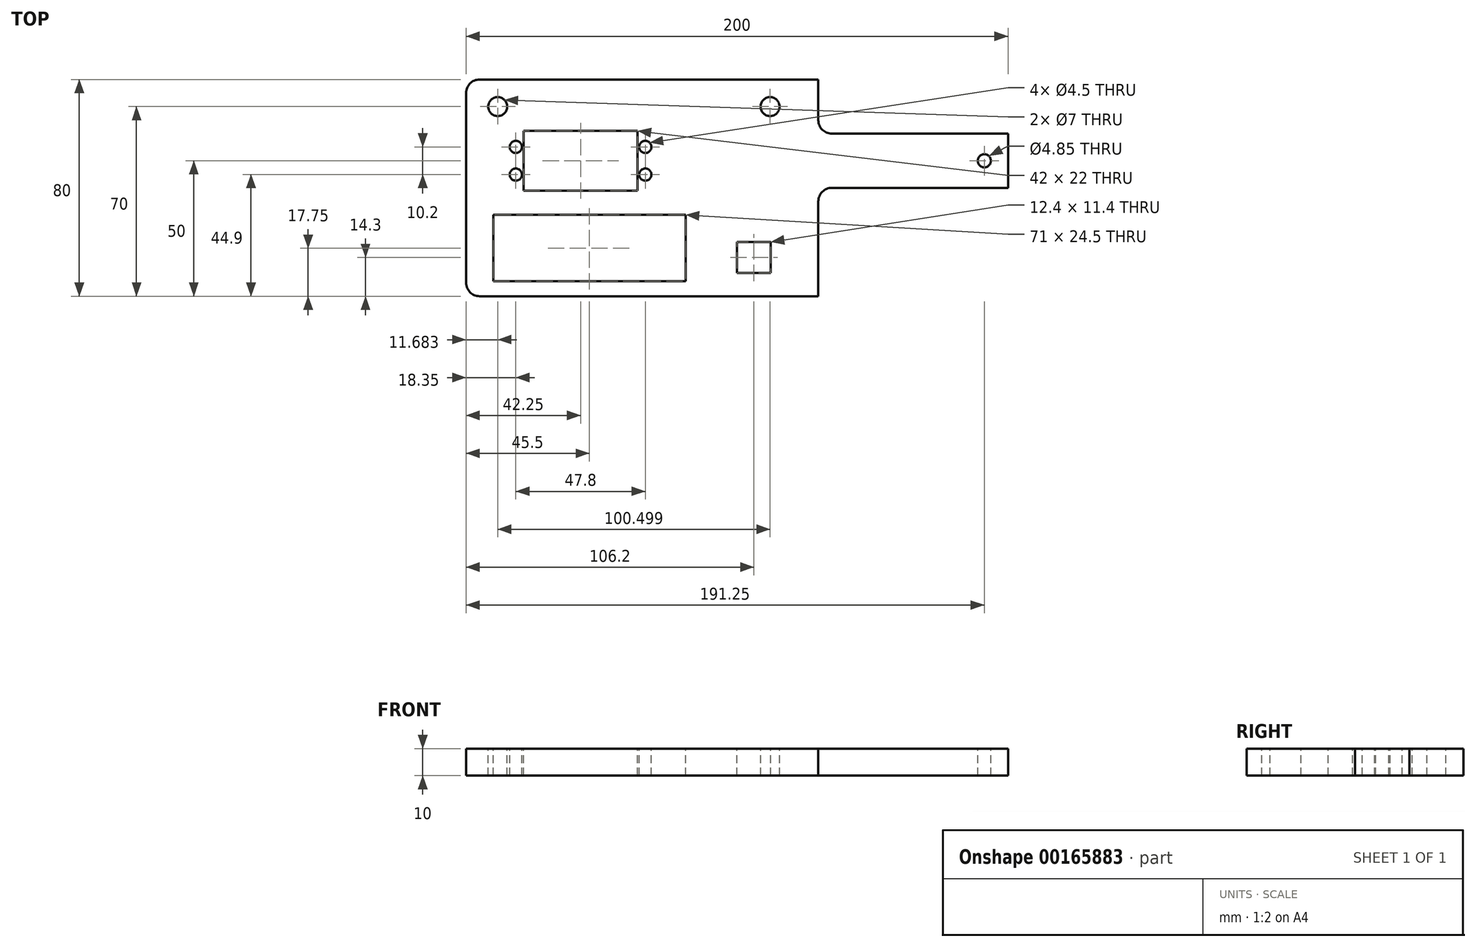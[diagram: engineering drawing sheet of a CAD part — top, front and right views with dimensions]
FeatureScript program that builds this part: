
annotation { "Feature Type Name" : "Feature", "Feature Type Description" : "" }
export const myFeature = defineFeature(function(context is Context, id is Id, definition is map)
    precondition{}
    {
        {
            var Q0;
            Q0=qCreatedBy(makeId("Top.planeOp"),FACE);
            var sketch = newSketch(context, id + "F0", { "sketchPlane" : qUnion([Q0])});
            skLineSegment(sketch, "E0.bottom", {"start": v(100, -40) * mm, "end": v(-100, -40) * mm});
            skLineSegment(sketch, "E0.top", {"start": v(100, 40) * mm, "end": v(-100, 40) * mm});
            skLineSegment(sketch, "E0.left", {"start": v(100, -40) * mm, "end": v(100, 40) * mm});
            skLineSegment(sketch, "E0.right", {"start": v(-100, -40) * mm, "end": v(-100, 40) * mm});
            skPoint(sketch, "E0.middle", {"position": v(0, 0) * mm});
            skSolve(sketch);
        }
        {
            var Q0;
            Q0=makeQuery(id+"F0.imprint","IMPRINT",FACE,{"disambiguationData":[TD([[makeQuery(id+"F0.imprint","IMPRINT",EDGE,{"derivedFrom":sQuery(id+"F0.wireOp",EDGE,"E0.bottom")}),-1.0]])]});
            extrude(context, id + "F1", {"entities" : qUnion([Q0]), "depth" : 10 * mm});
        }
        {
            var Q0;
            Q0=makeQuery(id+"F1.opExtrude","CAP_FACE",FACE,{"disambiguationData":[OSD([sQuery(id+"F0.wireOp",EDGE,"E0.bottom"),sQuery(id+"F0.wireOp",EDGE,"E0.top"),sQuery(id+"F0.wireOp",EDGE,"E0.left"),sQuery(id+"F0.wireOp",EDGE,"E0.right")])],"isStart":false});
            var sketch = newSketch(context, id + "F2", { "sketchPlane" : qUnion([Q0])});
            skLineSegment(sketch, "E1.bottom", {"start": v(-78.75, -1) * mm, "end": v(-36.75, -1) * mm});
            skLineSegment(sketch, "E1.top", {"start": v(-78.75, 21) * mm, "end": v(-36.75, 21) * mm});
            skLineSegment(sketch, "E1.left", {"start": v(-78.75, -1) * mm, "end": v(-78.75, 21) * mm});
            skLineSegment(sketch, "E1.right", {"start": v(-36.75, -1) * mm, "end": v(-36.75, 21) * mm});
            skPoint(sketch, "E1.middle", {"position": v(-57.75, 10) * mm});
            skSolve(sketch);
        }
        {
            var Q0;
            Q0=makeQuery(id+"F2.imprint","IMPRINT",FACE,{"disambiguationData":[TD([[makeQuery(id+"F2.imprint","IMPRINT",EDGE,{"derivedFrom":sQuery(id+"F2.wireOp",EDGE,"E1.bottom")}),1.0]])]});
            extrude(context, id + "F3", {"entities" : qUnion([Q0]), "operationType" : NewBodyOperationType.REMOVE, "endBound" : BoundingType.THROUGH_ALL, "oppositeDirection" : true, "depth" : 25 * mm});
        }
        {
            var Q0;
            Q0=makeQuery(id+"F1.opExtrude","CAP_FACE",FACE,{"disambiguationData":[OSD([sQuery(id+"F0.wireOp",EDGE,"E0.bottom"),sQuery(id+"F0.wireOp",EDGE,"E0.top"),sQuery(id+"F0.wireOp",EDGE,"E0.left"),sQuery(id+"F0.wireOp",EDGE,"E0.right")])],"isStart":false});
            var sketch = newSketch(context, id + "F4", { "sketchPlane" : qUnion([Q0])});
            skLineSegment(sketch, "E2.bottom", {"start": v(-81.65, 15.1) * mm, "end": v(-33.85, 15.1) * mm});
            skLineSegment(sketch, "E2.top", {"start": v(-81.65, 4.9) * mm, "end": v(-33.85, 4.9) * mm});
            skLineSegment(sketch, "E2.left", {"start": v(-81.65, 15.1) * mm, "end": v(-81.65, 4.9) * mm});
            skLineSegment(sketch, "E2.right", {"start": v(-33.85, 15.1) * mm, "end": v(-33.85, 4.9) * mm});
            skPoint(sketch, "E2.middle", {"position": v(-57.75, 10) * mm});
            skPoint(sketch, "E2.middle.positionSnap0", {"position": v(-78.75, 10) * mm});
            skPoint(sketch, "E2.middle.positionSnap1", {"position": v(-57.75, -1) * mm});
            skPoint(sketch, "E2.centerSnap0", {"position": v(-78.75, 10) * mm});
            skPoint(sketch, "E2.centerSnap1", {"position": v(-57.75, -1) * mm});
            skCircle(sketch, "E3", {"center": v(-81.65, 15.1) * mm, "radius": 2.25 * mm});
            skCircle(sketch, "E4", {"center": v(-81.65, 4.9) * mm, "radius": 2.25 * mm});
            skCircle(sketch, "E5", {"center": v(-33.85, 15.1) * mm, "radius": 2.25 * mm});
            skCircle(sketch, "E6", {"center": v(-33.85, 4.9) * mm, "radius": 2.25 * mm});
            skSolve(sketch);
        }
        {
            var Q0;
            {var subQ0=sQuery(id+"F4.wireOp",EDGE,"E2.left");var subQ1=sQuery(id+"F4.wireOp",EDGE,"E2.bottom");var subQ2=makeQuery(id+"F4.imprint","INTERSECT",VERTEX,{"derivedFrom":[subQ1,subQ0]});Q0=makeQuery(id+"F4.imprint","IMPRINT",FACE,{"disambiguationData":[TD([[makeQuery(id+"F4.imprint","IMPRINT",EDGE,{"disambiguationData":[TD([[subQ2,-1.0]])],"derivedFrom":subQ1}),1.0]])]});}
            var Q1;
            {var subQ0=sQuery(id+"F4.wireOp",EDGE,"E2.left");var subQ1=sQuery(id+"F4.wireOp",EDGE,"E2.bottom");var subQ2=makeQuery(id+"F4.imprint","INTERSECT",VERTEX,{"derivedFrom":[subQ1,subQ0]});Q1=makeQuery(id+"F4.imprint","IMPRINT",FACE,{"disambiguationData":[TD([[makeQuery(id+"F4.imprint","IMPRINT",EDGE,{"disambiguationData":[TD([[subQ2,-1.0]])],"derivedFrom":subQ1}),-1.0]])]});}
            var Q2;
            {var subQ0=sQuery(id+"F4.wireOp",EDGE,"E2.left");var subQ1=sQuery(id+"F4.wireOp",EDGE,"E2.top");var subQ2=makeQuery(id+"F4.imprint","INTERSECT",VERTEX,{"derivedFrom":[subQ1,subQ0]});Q2=makeQuery(id+"F4.imprint","IMPRINT",FACE,{"disambiguationData":[TD([[makeQuery(id+"F4.imprint","IMPRINT",EDGE,{"disambiguationData":[TD([[subQ2,-1.0]])],"derivedFrom":subQ1}),-1.0]])]});}
            var Q3;
            {var subQ0=sQuery(id+"F4.wireOp",EDGE,"E2.left");var subQ1=sQuery(id+"F4.wireOp",EDGE,"E2.top");var subQ2=makeQuery(id+"F4.imprint","INTERSECT",VERTEX,{"derivedFrom":[subQ1,subQ0]});Q3=makeQuery(id+"F4.imprint","IMPRINT",FACE,{"disambiguationData":[TD([[makeQuery(id+"F4.imprint","IMPRINT",EDGE,{"disambiguationData":[TD([[subQ2,-1.0]])],"derivedFrom":subQ1}),1.0]])]});}
            var Q4;
            {var subQ0=sQuery(id+"F4.wireOp",EDGE,"E2.right");var subQ1=sQuery(id+"F4.wireOp",EDGE,"E2.bottom");var subQ2=makeQuery(id+"F4.imprint","INTERSECT",VERTEX,{"derivedFrom":[subQ1,subQ0]});Q4=makeQuery(id+"F4.imprint","IMPRINT",FACE,{"disambiguationData":[TD([[makeQuery(id+"F4.imprint","IMPRINT",EDGE,{"disambiguationData":[TD([[subQ2,1.0]])],"derivedFrom":subQ1}),-1.0]])]});}
            var Q5;
            {var subQ0=sQuery(id+"F4.wireOp",EDGE,"E2.right");var subQ1=sQuery(id+"F4.wireOp",EDGE,"E2.bottom");var subQ2=makeQuery(id+"F4.imprint","INTERSECT",VERTEX,{"derivedFrom":[subQ1,subQ0]});Q5=makeQuery(id+"F4.imprint","IMPRINT",FACE,{"disambiguationData":[TD([[makeQuery(id+"F4.imprint","IMPRINT",EDGE,{"disambiguationData":[TD([[subQ2,1.0]])],"derivedFrom":subQ1}),1.0]])]});}
            var Q6;
            {var subQ0=sQuery(id+"F4.wireOp",EDGE,"E2.right");var subQ1=sQuery(id+"F4.wireOp",EDGE,"E2.top");var subQ2=makeQuery(id+"F4.imprint","INTERSECT",VERTEX,{"derivedFrom":[subQ1,subQ0]});Q6=makeQuery(id+"F4.imprint","IMPRINT",FACE,{"disambiguationData":[TD([[makeQuery(id+"F4.imprint","IMPRINT",EDGE,{"disambiguationData":[TD([[subQ2,1.0]])],"derivedFrom":subQ1}),1.0]])]});}
            var Q7;
            {var subQ0=sQuery(id+"F4.wireOp",EDGE,"E2.right");var subQ1=sQuery(id+"F4.wireOp",EDGE,"E2.top");var subQ2=makeQuery(id+"F4.imprint","INTERSECT",VERTEX,{"derivedFrom":[subQ1,subQ0]});Q7=makeQuery(id+"F4.imprint","IMPRINT",FACE,{"disambiguationData":[TD([[makeQuery(id+"F4.imprint","IMPRINT",EDGE,{"disambiguationData":[TD([[subQ2,1.0]])],"derivedFrom":subQ1}),-1.0]])]});}
            extrude(context, id + "F5", {"entities" : qUnion([Q0, Q1, Q2, Q3, Q4, Q5, Q6, Q7]), "operationType" : NewBodyOperationType.REMOVE, "endBound" : BoundingType.THROUGH_ALL, "oppositeDirection" : true, "depth" : 25 * mm});
        }
        {
            var Q0;
            Q0=makeQuery(id+"F1.opExtrude","CAP_FACE",FACE,{"disambiguationData":[OSD([sQuery(id+"F0.wireOp",EDGE,"E0.bottom"),sQuery(id+"F0.wireOp",EDGE,"E0.top"),sQuery(id+"F0.wireOp",EDGE,"E0.left"),sQuery(id+"F0.wireOp",EDGE,"E0.right")])],"isStart":false});
            var sketch = newSketch(context, id + "F6", { "sketchPlane" : qUnion([Q0])});
            skCircle(sketch, "E7", {"center": v(-88.32, 30) * mm, "radius": 3.5 * mm});
            skCircle(sketch, "E8", {"center": v(12.18, 30) * mm, "radius": 3.5 * mm});
            skSolve(sketch);
        }
        {
            var Q0;
            Q0=makeQuery(id+"F6.imprint","IMPRINT",FACE,{"disambiguationData":[TD([[makeQuery(id+"F6.imprint","IMPRINT",EDGE,{"derivedFrom":sQuery(id+"F6.wireOp",EDGE,"E7")}),1.0]])]});
            var Q1;
            Q1=makeQuery(id+"F6.imprint","IMPRINT",FACE,{"disambiguationData":[TD([[makeQuery(id+"F6.imprint","IMPRINT",EDGE,{"derivedFrom":sQuery(id+"F6.wireOp",EDGE,"E8")}),1.0]])]});
            extrude(context, id + "F7", {"entities" : qUnion([Q0, Q1]), "operationType" : NewBodyOperationType.REMOVE, "endBound" : BoundingType.THROUGH_ALL, "oppositeDirection" : true, "depth" : 25 * mm});
        }
        {
            var Q0;
            Q0=makeQuery(id+"F1.opExtrude","SWEPT_EDGE",EDGE,{"disambiguationData":[OSD([sQuery(id+"F0.wireOp",EDGE,"E0.top"),sQuery(id+"F0.wireOp",EDGE,"E0.right")])]});
            var Q1;
            Q1=makeQuery(id+"F1.opExtrude","SWEPT_EDGE",EDGE,{"disambiguationData":[OSD([sQuery(id+"F0.wireOp",EDGE,"E0.bottom"),sQuery(id+"F0.wireOp",EDGE,"E0.right")])]});
            var Q2;
            Q2=makeQuery(id+"F1.opExtrude","SWEPT_EDGE",EDGE,{"disambiguationData":[OSD([sQuery(id+"F0.wireOp",EDGE,"E0.top"),sQuery(id+"F0.wireOp",EDGE,"E0.left")])]});
            var Q3;
            Q3=makeQuery(id+"F1.opExtrude","SWEPT_EDGE",EDGE,{"disambiguationData":[OSD([sQuery(id+"F0.wireOp",EDGE,"E0.bottom"),sQuery(id+"F0.wireOp",EDGE,"E0.left")])]});
            fillet(context, id + "F8", {"entities" : qUnion([Q0, Q1, Q2, Q3]), "radius" : 5 * mm, "tangentPropagation" : true, "allowEdgeOverflow" : false});
        }
        {
            var Q0;
            Q0=makeQuery(id+"F1.opExtrude","CAP_FACE",FACE,{"disambiguationData":[OSD([sQuery(id+"F0.wireOp",EDGE,"E0.bottom"),sQuery(id+"F0.wireOp",EDGE,"E0.top"),sQuery(id+"F0.wireOp",EDGE,"E0.left"),sQuery(id+"F0.wireOp",EDGE,"E0.right")])],"isStart":false});
            var sketch = newSketch(context, id + "F9", { "sketchPlane" : qUnion([Q0])});
            skLineSegment(sketch, "E9.bottom", {"start": v(0, -20) * mm, "end": v(12.4, -20) * mm});
            skLineSegment(sketch, "E9.top", {"start": v(0, -31.4) * mm, "end": v(12.4, -31.4) * mm});
            skLineSegment(sketch, "E9.left", {"start": v(0, -20) * mm, "end": v(0, -31.4) * mm});
            skLineSegment(sketch, "E9.right", {"start": v(12.4, -20) * mm, "end": v(12.4, -31.4) * mm});
            skSolve(sketch);
        }
        {
            var Q0;
            Q0=makeQuery(id+"F1.opExtrude","CAP_FACE",FACE,{"disambiguationData":[OSD([sQuery(id+"F0.wireOp",EDGE,"E0.bottom"),sQuery(id+"F0.wireOp",EDGE,"E0.top"),sQuery(id+"F0.wireOp",EDGE,"E0.left"),sQuery(id+"F0.wireOp",EDGE,"E0.right")])],"isStart":false});
            var sketch = newSketch(context, id + "F10", { "sketchPlane" : qUnion([Q0])});
            skLineSegment(sketch, "E10.bottom", {"start": v(-78.75, 10) * mm, "end": v(91.25, 10) * mm});
            skLineSegment(sketch, "E10.top", {"start": v(-78.75, -40) * mm, "end": v(91.25, -40) * mm});
            skLineSegment(sketch, "E10.left", {"start": v(-78.75, 10) * mm, "end": v(-78.75, -40) * mm});
            skLineSegment(sketch, "E10.right", {"start": v(91.25, 10) * mm, "end": v(91.25, -40) * mm});
            skCircle(sketch, "E11", {"center": v(91.25, 10) * mm, "radius": 2.43 * mm});
            skSolve(sketch);
        }
        {
            var Q0;
            {var subQ0=sQuery(id+"F10.wireOp",EDGE,"E10.right");Q0=makeQuery(id+"F10.imprint","IMPRINT",FACE,{"disambiguationData":[TD([[makeQuery(id+"F10.imprint","IMPRINT",EDGE,{"derivedFrom":subQ0}),1.0]])]});}
            var sketch = newSketch(context, id + "F11", { "sketchPlane" : qUnion([Q0])});
            skLineSegment(sketch, "E12.bottom", {"start": v(100, 20) * mm, "end": v(30, 20) * mm});
            skLineSegment(sketch, "E12.top", {"start": v(100, 40) * mm, "end": v(30, 40) * mm});
            skLineSegment(sketch, "E12.left", {"start": v(100, 20) * mm, "end": v(100, 40) * mm});
            skLineSegment(sketch, "E12.right", {"start": v(30, 20) * mm, "end": v(30, 40) * mm});
            skLineSegment(sketch, "E13.bottom", {"start": v(30, 0) * mm, "end": v(100, 0) * mm});
            skLineSegment(sketch, "E13.top", {"start": v(30, -40) * mm, "end": v(100, -40) * mm});
            skLineSegment(sketch, "E13.left", {"start": v(30, 0) * mm, "end": v(30, -40) * mm});
            skLineSegment(sketch, "E13.right", {"start": v(100, 0) * mm, "end": v(100, -40) * mm});
            skSolve(sketch);
        }
        {
            var Q0;
            Q0=qSketchRegion(id+"F11",true);
            var Q1;
            {var subQ0=sQuery(id+"F10.wireOp",EDGE,"E10.right");var subQ1=sQuery(id+"F10.wireOp",EDGE,"E10.bottom");var subQ2=makeQuery(id+"F10.imprint","INTERSECT",VERTEX,{"derivedFrom":[subQ1,subQ0]});Q1=makeQuery(id+"F10.imprint","IMPRINT",FACE,{"disambiguationData":[TD([[makeQuery(id+"F10.imprint","IMPRINT",EDGE,{"disambiguationData":[TD([[subQ2,1.0]])],"derivedFrom":subQ1}),1.0]])]});}
            var Q2;
            {var subQ0=sQuery(id+"F10.wireOp",EDGE,"E10.right");var subQ1=sQuery(id+"F10.wireOp",EDGE,"E10.bottom");var subQ2=makeQuery(id+"F10.imprint","INTERSECT",VERTEX,{"derivedFrom":[subQ1,subQ0]});Q2=makeQuery(id+"F10.imprint","IMPRINT",FACE,{"disambiguationData":[TD([[makeQuery(id+"F10.imprint","IMPRINT",EDGE,{"disambiguationData":[TD([[subQ2,1.0]])],"derivedFrom":subQ1}),-1.0]])]});}
            var Q3;
            Q3=makeQuery(id+"F9.imprint","IMPRINT",FACE,{"disambiguationData":[TD([[makeQuery(id+"F9.imprint","IMPRINT",EDGE,{"derivedFrom":sQuery(id+"F9.wireOp",EDGE,"E9.bottom")}),-1.0]])]});
            extrude(context, id + "F12", {"entities" : qUnion([Q0, Q1, Q2, Q3]), "operationType" : NewBodyOperationType.REMOVE, "endBound" : BoundingType.THROUGH_ALL, "oppositeDirection" : true, "depth" : 25 * mm});
        }
        {
            var Q0;
            Q0=makeQuery(id+"F12.boolean.opBoolean","COPY",EDGE,{"derivedFrom":makeQuery(id+"F12.opExtrude","SWEPT_EDGE",EDGE,{"disambiguationData":[OSD([sQuery(id+"F0.wireOp",EDGE,"E0.top"),sQuery(id+"F11.wireOp",EDGE,"E12.top"),sQuery(id+"F11.wireOp",EDGE,"E12.right")])]})});
            var Q1;
            Q1=makeQuery(id+"F12.boolean.opBoolean","COPY",EDGE,{"derivedFrom":makeQuery(id+"F12.opExtrude","SWEPT_EDGE",EDGE,{"disambiguationData":[OSD([sQuery(id+"F11.wireOp",EDGE,"E12.bottom"),sQuery(id+"F11.wireOp",EDGE,"E12.right")])]})});
            var Q2;
            Q2=makeQuery(id+"F12.boolean.opBoolean","COPY",EDGE,{"derivedFrom":makeQuery(id+"F12.opExtrude","SWEPT_EDGE",EDGE,{"disambiguationData":[OSD([sQuery(id+"F0.wireOp",EDGE,"E0.left"),sQuery(id+"F11.wireOp",EDGE,"E12.bottom"),sQuery(id+"F11.wireOp",EDGE,"E12.left")])]})});
            var Q3;
            Q3=makeQuery(id+"F12.boolean.opBoolean","COPY",EDGE,{"derivedFrom":makeQuery(id+"F12.opExtrude","SWEPT_EDGE",EDGE,{"disambiguationData":[OSD([sQuery(id+"F11.wireOp",EDGE,"E13.top"),sQuery(id+"F11.wireOp",EDGE,"E13.left")])]})});
            var Q4;
            Q4=makeQuery(id+"F12.boolean.opBoolean","COPY",EDGE,{"derivedFrom":makeQuery(id+"F12.opExtrude","SWEPT_EDGE",EDGE,{"disambiguationData":[OSD([sQuery(id+"F11.wireOp",EDGE,"E13.bottom"),sQuery(id+"F11.wireOp",EDGE,"E13.right")])]})});
            var Q5;
            Q5=makeQuery(id+"F12.boolean.opBoolean","COPY",EDGE,{"derivedFrom":makeQuery(id+"F12.opExtrude","SWEPT_EDGE",EDGE,{"disambiguationData":[OSD([sQuery(id+"F11.wireOp",EDGE,"E13.bottom"),sQuery(id+"F11.wireOp",EDGE,"E13.left")])]})});
            fillet(context, id + "F13", {"entities" : qUnion([Q0, Q1, Q2, Q3, Q4, Q5]), "radius" : 5 * mm, "tangentPropagation" : true, "allowEdgeOverflow" : false});
        }
        {
            var Q0;
            Q0=makeQuery(id+"F9.imprint","IMPRINT",FACE,{"disambiguationData":[TD([[makeQuery(id+"F9.imprint","IMPRINT",EDGE,{"derivedFrom":sQuery(id+"F9.wireOp",EDGE,"E9.bottom")}),1.0]])]});
            var sketch = newSketch(context, id + "F14", { "sketchPlane" : qUnion([Q0])});
            skLineSegment(sketch, "E14.bottom", {"start": v(-90, -10) * mm, "end": v(-19, -10) * mm});
            skLineSegment(sketch, "E14.top", {"start": v(-90, -34.5) * mm, "end": v(-19, -34.5) * mm});
            skLineSegment(sketch, "E14.left", {"start": v(-90, -10) * mm, "end": v(-90, -34.5) * mm});
            skLineSegment(sketch, "E14.right", {"start": v(-19, -10) * mm, "end": v(-19, -34.5) * mm});
            skSolve(sketch);
        }
        {
            var Q0;
            Q0=makeQuery(id+"F14.imprint","IMPRINT",FACE,{"disambiguationData":[TD([[makeQuery(id+"F14.imprint","IMPRINT",EDGE,{"derivedFrom":sQuery(id+"F14.wireOp",EDGE,"E14.bottom")}),-1.0]])]});
            extrude(context, id + "F15", {"entities" : qUnion([Q0]), "operationType" : NewBodyOperationType.REMOVE, "endBound" : BoundingType.THROUGH_ALL, "oppositeDirection" : true, "depth" : 25 * mm});
        }
    });
